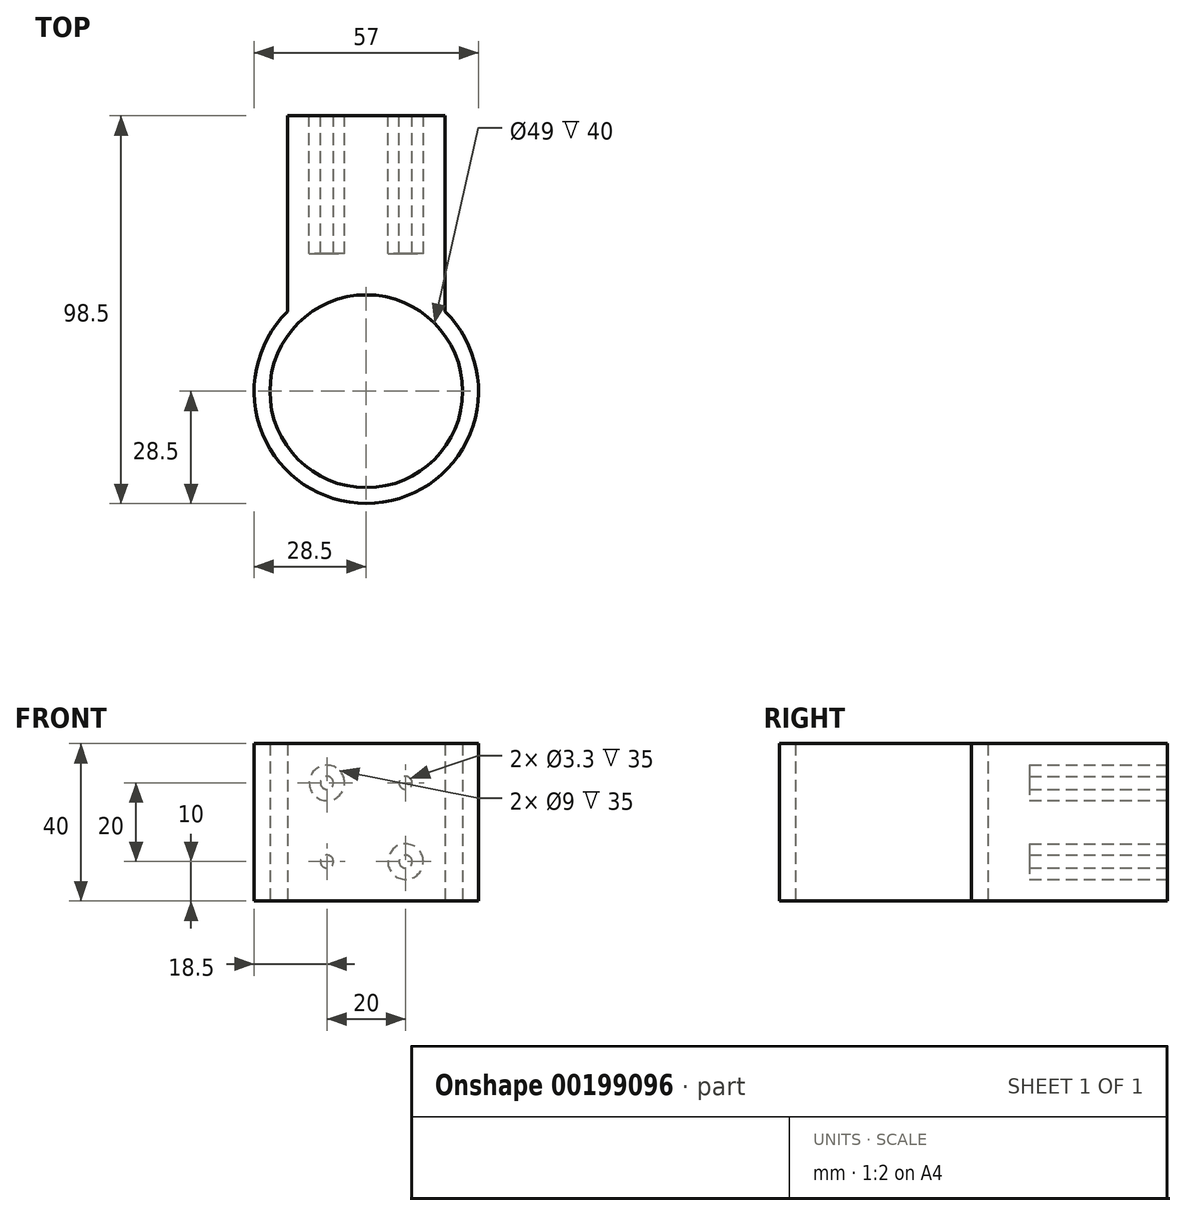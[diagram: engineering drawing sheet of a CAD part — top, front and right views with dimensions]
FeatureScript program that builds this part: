
annotation { "Feature Type Name" : "Feature", "Feature Type Description" : "" }
export const myFeature = defineFeature(function(context is Context, id is Id, definition is map)
    precondition{}
    {
        {
            var Q0;
            Q0=qCreatedBy(makeId("Top.planeOp"),FACE);
            var sketch = newSketch(context, id + "F0", { "sketchPlane" : qUnion([Q0])});
            skLineSegment(sketch, "E0.bottom", {"start": v(-20, 70) * mm, "end": v(20, 70) * mm});
            skLineSegment(sketch, "E0.top", {"start": v(-20, 0) * mm, "end": v(20, 0) * mm, "construction": true});
            skLineSegment(sketch, "E0.left", {"start": v(-20, 70) * mm, "end": v(-20, 20.3) * mm});
            skLineSegment(sketch, "E0.right", {"start": v(20, 70) * mm, "end": v(20, 20.3) * mm});
            skCircle(sketch, "E1", {"center": v(0, 0) * mm, "radius": 24.5 * mm});
            skPoint(sketch, "E2", {"position": v(-20, 20.3) * mm});
            skPoint(sketch, "E3", {"position": v(20, 20.3) * mm});
            skLineSegment(sketch, "E4", {"start": v(20, 0) * mm, "end": v(36.53, 0) * mm, "construction": true});
            skLineSegment(sketch, "E5", {"start": v(20, 70) * mm, "end": v(36.53, 70) * mm, "construction": true});
            skLineSegment(sketch, "E6", {"start": v(36.53, 0) * mm, "end": v(36.53, 70) * mm, "construction": true});
            skArc(sketch, "E7", {"start": v(-20, 20.3) * mm, "mid": v(0, -28.5) * mm, "end": v(20, 20.3) * mm});
            skSolve(sketch);
        }
        {
            var Q0;
            Q0 = qSketchRegion(id + "F0", true);
            extrude(context, id + "F1", {"entities" : qUnion([Q0]), "depth" : 40 * mm});
        }
        {
            var Q0;
            Q0=makeQuery(id+"F1.opExtrude","SWEPT_FACE",FACE,{"disambiguationData":[OSD([sQuery(id+"F0.wireOp",EDGE,"E0.bottom")])]});
            var sketch = newSketch(context, id + "F2", { "sketchPlane" : qUnion([Q0])});
            skCircle(sketch, "E8", {"center": v(-10, 30) * mm, "radius": 1.65 * mm});
            skLineSegment(sketch, "E9", {"start": v(-10, 40) * mm, "end": v(-10, 30) * mm, "construction": true});
            skLineSegment(sketch, "E10", {"start": v(-20, 30) * mm, "end": v(-10, 30) * mm, "construction": true});
            skCircle(sketch, "E11.0", {"center": v(-10, 30) * mm, "radius": 4.5 * mm});
            skLineSegment(sketch, "E12", {"start": v(-20, 20) * mm, "end": v(20, 20) * mm});
            skCircle(sketch, "E13.MirrorC", {"center": v(-10, 10) * mm, "radius": 4.5 * mm});
            skCircle(sketch, "E14.MirrorC", {"center": v(-10, 10) * mm, "radius": 1.65 * mm});
            skCircle(sketch, "E15.MirrorC", {"center": v(10, 30) * mm, "radius": 4.5 * mm});
            skCircle(sketch, "E16.MirrorC", {"center": v(10, 30) * mm, "radius": 1.65 * mm});
            skCircle(sketch, "E17.MirrorC", {"center": v(10, 10) * mm, "radius": 4.5 * mm});
            skCircle(sketch, "E18.MirrorC", {"center": v(10, 10) * mm, "radius": 1.65 * mm});
            skSolve(sketch);
        }
        {
            var Q0;
            Q0=makeQuery(id+"F2.imprint","IMPRINT",FACE,{"disambiguationData":[TD([[makeQuery(id+"F2.imprint","IMPRINT",EDGE,{"derivedFrom":sQuery(id+"F2.wireOp",EDGE,"E8")}),1.0]])]});
            var Q1;
            Q1=makeQuery(id+"F2.imprint","IMPRINT",FACE,{"disambiguationData":[TD([[makeQuery(id+"F2.imprint","IMPRINT",EDGE,{"derivedFrom":sQuery(id+"F2.wireOp",EDGE,"E16.MirrorC")}),-1.0]])]});
            var Q2;
            Q2=makeQuery(id+"F2.imprint","IMPRINT",FACE,{"disambiguationData":[TD([[makeQuery(id+"F2.imprint","IMPRINT",EDGE,{"derivedFrom":sQuery(id+"F2.wireOp",EDGE,"E18.MirrorC")}),1.0]])]});
            var Q3;
            Q3=makeQuery(id+"F2.imprint","IMPRINT",FACE,{"disambiguationData":[TD([[makeQuery(id+"F2.imprint","IMPRINT",EDGE,{"derivedFrom":sQuery(id+"F2.wireOp",EDGE,"E14.MirrorC")}),-1.0]])]});
            var Q4;
            Q4=sQuery(id+"F2.wireOp",EDGE,"E8");
            var Q5;
            Q5=sQuery(id+"F2.wireOp",EDGE,"E14.MirrorC");
            var Q6;
            Q6=sQuery(id+"F2.wireOp",EDGE,"E16.MirrorC");
            var Q7;
            Q7=sQuery(id+"F2.wireOp",EDGE,"E18.MirrorC");
            extrude(context, id + "F3", {"entities" : qUnion([Q0, Q1, Q2, Q3]), "operationType" : NewBodyOperationType.REMOVE, "surfaceEntities" : qUnion([Q4, Q5, Q6, Q7]), "oppositeDirection" : true, "depth" : 35 * mm});
        }
    });
